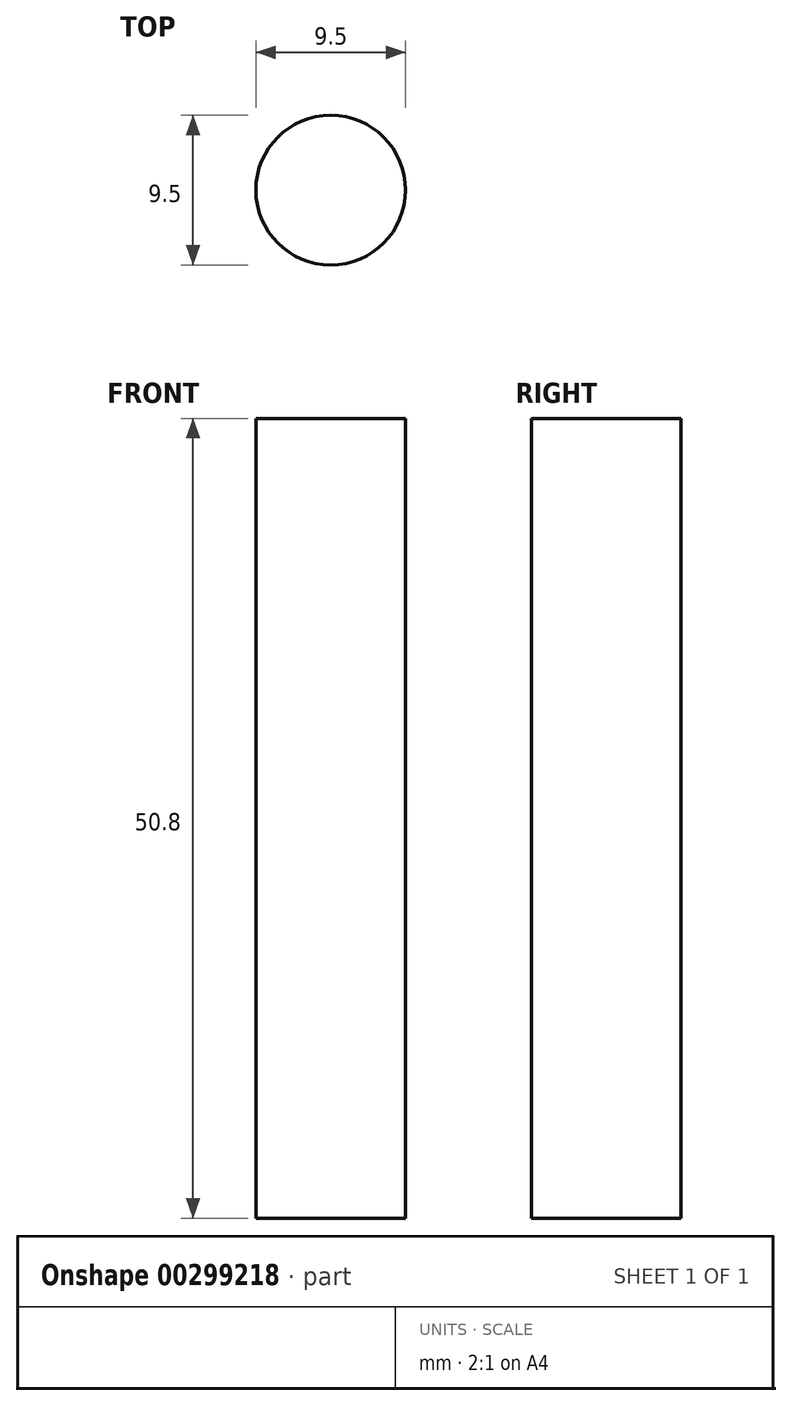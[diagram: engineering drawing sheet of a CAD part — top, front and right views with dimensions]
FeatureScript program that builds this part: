
annotation { "Feature Type Name" : "Feature", "Feature Type Description" : "" }
export const myFeature = defineFeature(function(context is Context, id is Id, definition is map)
    precondition{}
    {
        {
            var Q0;
            Q0=qCreatedBy(makeId("Top.planeOp"),FACE);
            var sketch = newSketch(context, id + "F0", { "sketchPlane" : qUnion([Q0])});
            skCircle(sketch, "E0", {"center": v(0, 0) * mm, "radius": 4.75 * mm});
            skSolve(sketch);
        }
        {
            var Q0;
            Q0=makeQuery(id+"F0.imprint","IMPRINT",FACE,{"disambiguationData":[TD([[makeQuery(id+"F0.imprint","IMPRINT",EDGE,{"derivedFrom":sQuery(id+"F0.wireOp",EDGE,"E0")}),1.0]])]});
            extrude(context, id + "F1", {"entities" : qUnion([Q0]), "depth" : 50.8 * mm});
        }
    });
